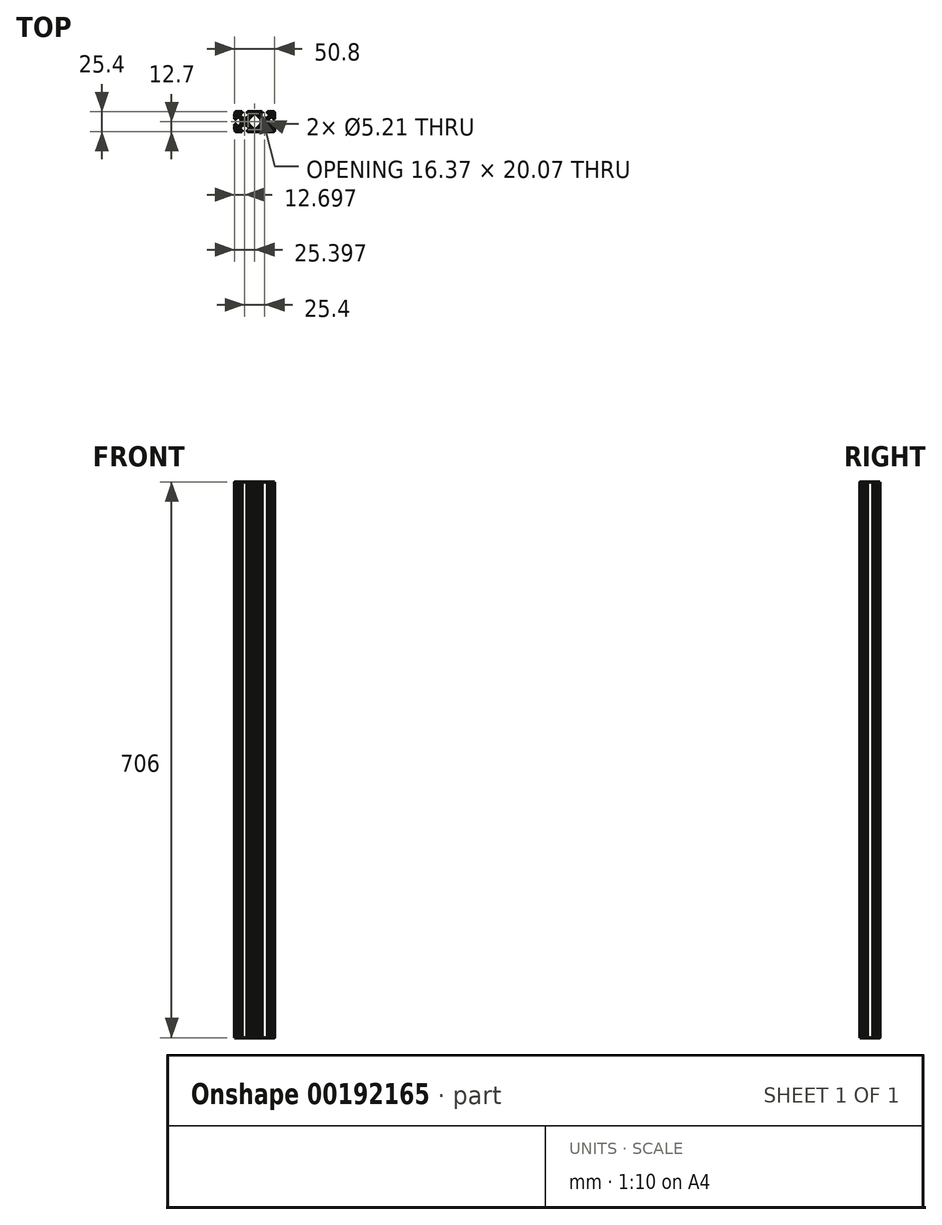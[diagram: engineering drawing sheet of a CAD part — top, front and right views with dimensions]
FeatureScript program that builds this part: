
annotation { "Feature Type Name" : "Feature", "Feature Type Description" : "" }
export const myFeature = defineFeature(function(context is Context, id is Id, definition is map)
    precondition{}
    {
        {
            var Q0;
            Q0=qCreatedBy(makeId("Top.planeOp"),FACE);
            var sketch = newSketch(context, id + "F0", { "sketchPlane" : qUnion([Q0])});
            skArc(sketch, "E0.0.0", {"start": v(22.53, 3.34) * mm, "mid": v(24.02, 3.96) * mm, "end": v(24.64, 5.45) * mm});
            skLineSegment(sketch, "E0.0.1", {"start": v(24.64, 5.45) * mm, "end": v(24.64, 5.47) * mm});
            skArc(sketch, "E0.0.2", {"start": v(24.64, 5.47) * mm, "mid": v(24.13, 5.98) * mm, "end": v(24.64, 6.49) * mm});
            skLineSegment(sketch, "E0.0.3", {"start": v(24.64, 6.49) * mm, "end": v(24.64, 9.72) * mm});
            skArc(sketch, "E0.0.4", {"start": v(24.64, 9.72) * mm, "mid": v(24.13, 10.22) * mm, "end": v(24.64, 10.73) * mm});
            skLineSegment(sketch, "E0.0.5", {"start": v(24.64, 10.73) * mm, "end": v(24.64, 11.68) * mm});
            skArc(sketch, "E0.0.6", {"start": v(24.64, 11.68) * mm, "mid": v(23.53, 12.79) * mm, "end": v(22.43, 11.68) * mm});
            skLineSegment(sketch, "E0.0.7", {"start": v(22.43, 11.68) * mm, "end": v(22.43, 9.67) * mm});
            skArc(sketch, "E0.0.8", {"start": v(22.43, 9.67) * mm, "mid": v(21.77, 8.7) * mm, "end": v(20.62, 8.92) * mm});
            skLineSegment(sketch, "E0.0.9", {"start": v(20.62, 8.92) * mm, "end": v(17.38, 12.16) * mm});
            skArc(sketch, "E0.0.10", {"start": v(17.38, 12.16) * mm, "mid": v(16.7, 13.19) * mm, "end": v(16.45, 14.4) * mm});
            skLineSegment(sketch, "E0.0.11", {"start": v(16.45, 14.4) * mm, "end": v(16.45, 17.68) * mm});
            skArc(sketch, "E0.0.12", {"start": v(16.45, 17.68) * mm, "mid": v(16.7, 18.9) * mm, "end": v(17.38, 19.92) * mm});
            skLineSegment(sketch, "E0.0.13", {"start": v(17.38, 19.92) * mm, "end": v(20.62, 23.16) * mm});
            skArc(sketch, "E0.0.14", {"start": v(20.62, 23.16) * mm, "mid": v(21.77, 23.39) * mm, "end": v(22.43, 22.41) * mm});
            skLineSegment(sketch, "E0.0.15", {"start": v(22.43, 22.41) * mm, "end": v(22.43, 20.4) * mm});
            skArc(sketch, "E0.0.16", {"start": v(22.43, 20.4) * mm, "mid": v(23.53, 19.3) * mm, "end": v(24.64, 20.4) * mm});
            skLineSegment(sketch, "E0.0.17", {"start": v(24.64, 20.4) * mm, "end": v(24.64, 21.35) * mm});
            skArc(sketch, "E0.0.18", {"start": v(24.64, 21.35) * mm, "mid": v(24.13, 21.86) * mm, "end": v(24.64, 22.36) * mm});
            skLineSegment(sketch, "E0.0.19", {"start": v(24.64, 22.36) * mm, "end": v(24.64, 25.6) * mm});
            skArc(sketch, "E0.0.20", {"start": v(24.64, 25.6) * mm, "mid": v(24.13, 26.1) * mm, "end": v(24.64, 26.6) * mm});
            skLineSegment(sketch, "E0.0.21", {"start": v(24.64, 26.6) * mm, "end": v(24.64, 26.63) * mm});
            skArc(sketch, "E0.0.22", {"start": v(24.64, 26.63) * mm, "mid": v(24.02, 28.12) * mm, "end": v(22.53, 28.74) * mm});
            skLineSegment(sketch, "E0.0.23", {"start": v(22.53, 28.74) * mm, "end": v(22.5, 28.74) * mm});
            skArc(sketch, "E0.0.24", {"start": v(22.5, 28.74) * mm, "mid": v(22, 28.23) * mm, "end": v(21.49, 28.74) * mm});
            skLineSegment(sketch, "E0.0.25", {"start": v(21.49, 28.74) * mm, "end": v(18.26, 28.74) * mm});
            skArc(sketch, "E0.0.26", {"start": v(18.26, 28.74) * mm, "mid": v(17.75, 28.23) * mm, "end": v(17.25, 28.74) * mm});
            skLineSegment(sketch, "E0.0.27", {"start": v(17.25, 28.74) * mm, "end": v(16.3, 28.74) * mm});
            skArc(sketch, "E0.0.28", {"start": v(16.3, 28.74) * mm, "mid": v(15.19, 27.64) * mm, "end": v(16.3, 26.53) * mm});
            skLineSegment(sketch, "E0.0.29", {"start": v(16.3, 26.53) * mm, "end": v(18.3, 26.53) * mm});
            skArc(sketch, "E0.0.30", {"start": v(18.3, 26.53) * mm, "mid": v(19.29, 25.88) * mm, "end": v(19.06, 24.72) * mm});
            skLineSegment(sketch, "E0.0.31", {"start": v(19.06, 24.72) * mm, "end": v(15.82, 21.49) * mm});
            skArc(sketch, "E0.0.32", {"start": v(15.82, 21.49) * mm, "mid": v(14.8, 20.8) * mm, "end": v(13.58, 20.56) * mm});
            skLineSegment(sketch, "E0.0.33", {"start": v(13.58, 20.56) * mm, "end": v(10.3, 20.56) * mm});
            skArc(sketch, "E0.0.34", {"start": v(10.3, 20.56) * mm, "mid": v(9.08, 20.8) * mm, "end": v(8.05, 21.49) * mm});
            skLineSegment(sketch, "E0.0.35", {"start": v(8.05, 21.49) * mm, "end": v(4.82, 24.72) * mm});
            skArc(sketch, "E0.0.36", {"start": v(4.82, 24.72) * mm, "mid": v(4.59, 25.88) * mm, "end": v(5.57, 26.53) * mm});
            skLineSegment(sketch, "E0.0.37", {"start": v(5.57, 26.53) * mm, "end": v(7.58, 26.53) * mm});
            skArc(sketch, "E0.0.38", {"start": v(7.58, 26.53) * mm, "mid": v(8.69, 27.64) * mm, "end": v(7.58, 28.74) * mm});
            skLineSegment(sketch, "E0.0.39", {"start": v(7.58, 28.74) * mm, "end": v(6.63, 28.74) * mm});
            skArc(sketch, "E0.0.40", {"start": v(6.63, 28.74) * mm, "mid": v(6.12, 28.23) * mm, "end": v(5.61, 28.74) * mm});
            skLineSegment(sketch, "E0.0.41", {"start": v(5.61, 28.74) * mm, "end": v(2.39, 28.74) * mm});
            skArc(sketch, "E0.0.42", {"start": v(2.39, 28.74) * mm, "mid": v(1.88, 28.23) * mm, "end": v(1.37, 28.74) * mm});
            skLineSegment(sketch, "E0.0.43", {"start": v(1.37, 28.74) * mm, "end": v(-2.9, 28.74) * mm});
            skArc(sketch, "E0.0.44", {"start": v(-2.9, 28.74) * mm, "mid": v(-3.4, 28.23) * mm, "end": v(-3.91, 28.74) * mm});
            skLineSegment(sketch, "E0.0.45", {"start": v(-3.91, 28.74) * mm, "end": v(-7.14, 28.74) * mm});
            skArc(sketch, "E0.0.46", {"start": v(-7.14, 28.74) * mm, "mid": v(-7.65, 28.23) * mm, "end": v(-8.15, 28.74) * mm});
            skLineSegment(sketch, "E0.0.47", {"start": v(-8.15, 28.74) * mm, "end": v(-9.1, 28.74) * mm});
            skArc(sketch, "E0.0.48", {"start": v(-9.1, 28.74) * mm, "mid": v(-10.21, 27.64) * mm, "end": v(-9.1, 26.53) * mm});
            skLineSegment(sketch, "E0.0.49", {"start": v(-9.1, 26.53) * mm, "end": v(-7.1, 26.53) * mm});
            skArc(sketch, "E0.0.50", {"start": v(-7.1, 26.53) * mm, "mid": v(-6.11, 25.88) * mm, "end": v(-6.34, 24.72) * mm});
            skLineSegment(sketch, "E0.0.51", {"start": v(-6.34, 24.72) * mm, "end": v(-9.58, 21.49) * mm});
            skArc(sketch, "E0.0.52", {"start": v(-9.58, 21.49) * mm, "mid": v(-10.6, 20.8) * mm, "end": v(-11.82, 20.56) * mm});
            skLineSegment(sketch, "E0.0.53", {"start": v(-11.82, 20.56) * mm, "end": v(-15.1, 20.56) * mm});
            skArc(sketch, "E0.0.54", {"start": v(-15.1, 20.56) * mm, "mid": v(-16.32, 20.8) * mm, "end": v(-17.35, 21.49) * mm});
            skLineSegment(sketch, "E0.0.55", {"start": v(-17.35, 21.49) * mm, "end": v(-20.58, 24.72) * mm});
            skArc(sketch, "E0.0.56", {"start": v(-20.58, 24.72) * mm, "mid": v(-20.81, 25.88) * mm, "end": v(-19.83, 26.53) * mm});
            skLineSegment(sketch, "E0.0.57", {"start": v(-19.83, 26.53) * mm, "end": v(-17.82, 26.53) * mm});
            skArc(sketch, "E0.0.58", {"start": v(-17.82, 26.53) * mm, "mid": v(-16.71, 27.64) * mm, "end": v(-17.82, 28.74) * mm});
            skLineSegment(sketch, "E0.0.59", {"start": v(-17.82, 28.74) * mm, "end": v(-18.77, 28.74) * mm});
            skArc(sketch, "E0.0.60", {"start": v(-18.77, 28.74) * mm, "mid": v(-19.28, 28.23) * mm, "end": v(-19.79, 28.74) * mm});
            skLineSegment(sketch, "E0.0.61", {"start": v(-19.79, 28.74) * mm, "end": v(-23.01, 28.74) * mm});
            skArc(sketch, "E0.0.62", {"start": v(-23.01, 28.74) * mm, "mid": v(-23.52, 28.23) * mm, "end": v(-24.03, 28.74) * mm});
            skLineSegment(sketch, "E0.0.63", {"start": v(-24.03, 28.74) * mm, "end": v(-24.05, 28.74) * mm});
            skArc(sketch, "E0.0.64", {"start": v(-24.05, 28.74) * mm, "mid": v(-25.55, 28.12) * mm, "end": v(-26.16, 26.63) * mm});
            skLineSegment(sketch, "E0.0.65", {"start": v(-26.16, 26.63) * mm, "end": v(-26.16, 26.6) * mm});
            skArc(sketch, "E0.0.66", {"start": v(-26.16, 26.6) * mm, "mid": v(-25.65, 26.1) * mm, "end": v(-26.16, 25.6) * mm});
            skLineSegment(sketch, "E0.0.67", {"start": v(-26.16, 25.6) * mm, "end": v(-26.16, 22.36) * mm});
            skArc(sketch, "E0.0.68", {"start": v(-26.16, 22.36) * mm, "mid": v(-25.65, 21.86) * mm, "end": v(-26.16, 21.35) * mm});
            skLineSegment(sketch, "E0.0.69", {"start": v(-26.16, 21.35) * mm, "end": v(-26.16, 20.4) * mm});
            skArc(sketch, "E0.0.70", {"start": v(-26.16, 20.4) * mm, "mid": v(-25.06, 19.3) * mm, "end": v(-23.95, 20.4) * mm});
            skLineSegment(sketch, "E0.0.71", {"start": v(-23.95, 20.4) * mm, "end": v(-23.95, 22.41) * mm});
            skArc(sketch, "E0.0.72", {"start": v(-23.95, 22.41) * mm, "mid": v(-23.3, 23.39) * mm, "end": v(-22.14, 23.16) * mm});
            skLineSegment(sketch, "E0.0.73", {"start": v(-22.14, 23.16) * mm, "end": v(-18.91, 19.92) * mm});
            skArc(sketch, "E0.0.74", {"start": v(-18.91, 19.92) * mm, "mid": v(-18.22, 18.9) * mm, "end": v(-17.98, 17.68) * mm});
            skLineSegment(sketch, "E0.0.75", {"start": v(-17.98, 17.68) * mm, "end": v(-17.98, 14.4) * mm});
            skArc(sketch, "E0.0.76", {"start": v(-17.98, 14.4) * mm, "mid": v(-18.22, 13.19) * mm, "end": v(-18.91, 12.16) * mm});
            skLineSegment(sketch, "E0.0.77", {"start": v(-18.91, 12.16) * mm, "end": v(-22.14, 8.92) * mm});
            skArc(sketch, "E0.0.78", {"start": v(-22.14, 8.92) * mm, "mid": v(-23.3, 8.7) * mm, "end": v(-23.95, 9.67) * mm});
            skLineSegment(sketch, "E0.0.79", {"start": v(-23.95, 9.67) * mm, "end": v(-23.95, 11.68) * mm});
            skArc(sketch, "E0.0.80", {"start": v(-23.95, 11.68) * mm, "mid": v(-25.06, 12.79) * mm, "end": v(-26.16, 11.68) * mm});
            skLineSegment(sketch, "E0.0.81", {"start": v(-26.16, 11.68) * mm, "end": v(-26.16, 10.73) * mm});
            skArc(sketch, "E0.0.82", {"start": v(-26.16, 10.73) * mm, "mid": v(-25.65, 10.22) * mm, "end": v(-26.16, 9.72) * mm});
            skLineSegment(sketch, "E0.0.83", {"start": v(-26.16, 9.72) * mm, "end": v(-26.16, 6.49) * mm});
            skArc(sketch, "E0.0.84", {"start": v(-26.16, 6.49) * mm, "mid": v(-25.65, 5.98) * mm, "end": v(-26.16, 5.47) * mm});
            skLineSegment(sketch, "E0.0.85", {"start": v(-26.16, 5.47) * mm, "end": v(-26.16, 5.45) * mm});
            skArc(sketch, "E0.0.86", {"start": v(-26.16, 5.45) * mm, "mid": v(-25.55, 3.96) * mm, "end": v(-24.05, 3.34) * mm});
            skLineSegment(sketch, "E0.0.87", {"start": v(-24.05, 3.34) * mm, "end": v(-24.03, 3.34) * mm});
            skArc(sketch, "E0.0.88", {"start": v(-24.03, 3.34) * mm, "mid": v(-23.52, 3.85) * mm, "end": v(-23.01, 3.34) * mm});
            skLineSegment(sketch, "E0.0.89", {"start": v(-23.01, 3.34) * mm, "end": v(-19.79, 3.34) * mm});
            skArc(sketch, "E0.0.90", {"start": v(-19.79, 3.34) * mm, "mid": v(-19.28, 3.85) * mm, "end": v(-18.77, 3.34) * mm});
            skLineSegment(sketch, "E0.0.91", {"start": v(-18.77, 3.34) * mm, "end": v(-17.82, 3.34) * mm});
            skArc(sketch, "E0.0.92", {"start": v(-17.82, 3.34) * mm, "mid": v(-16.71, 4.45) * mm, "end": v(-17.82, 5.55) * mm});
            skLineSegment(sketch, "E0.0.93", {"start": v(-17.82, 5.55) * mm, "end": v(-19.83, 5.55) * mm});
            skArc(sketch, "E0.0.94", {"start": v(-19.83, 5.55) * mm, "mid": v(-20.81, 6.2) * mm, "end": v(-20.58, 7.36) * mm});
            skLineSegment(sketch, "E0.0.95", {"start": v(-20.58, 7.36) * mm, "end": v(-17.35, 10.6) * mm});
            skArc(sketch, "E0.0.96", {"start": v(-17.35, 10.6) * mm, "mid": v(-16.32, 11.28) * mm, "end": v(-15.1, 11.52) * mm});
            skLineSegment(sketch, "E0.0.97", {"start": v(-15.1, 11.52) * mm, "end": v(-11.82, 11.52) * mm});
            skArc(sketch, "E0.0.98", {"start": v(-11.82, 11.52) * mm, "mid": v(-10.6, 11.28) * mm, "end": v(-9.58, 10.6) * mm});
            skLineSegment(sketch, "E0.0.99", {"start": v(-9.58, 10.6) * mm, "end": v(-6.34, 7.36) * mm});
            skArc(sketch, "E0.0.100", {"start": v(-6.34, 7.36) * mm, "mid": v(-6.11, 6.2) * mm, "end": v(-7.1, 5.55) * mm});
            skLineSegment(sketch, "E0.0.101", {"start": v(-7.1, 5.55) * mm, "end": v(-9.1, 5.55) * mm});
            skArc(sketch, "E0.0.102", {"start": v(-9.1, 5.55) * mm, "mid": v(-10.21, 4.45) * mm, "end": v(-9.1, 3.34) * mm});
            skLineSegment(sketch, "E0.0.103", {"start": v(-9.1, 3.34) * mm, "end": v(-8.15, 3.34) * mm});
            skArc(sketch, "E0.0.104", {"start": v(-8.15, 3.34) * mm, "mid": v(-7.65, 3.85) * mm, "end": v(-7.14, 3.34) * mm});
            skLineSegment(sketch, "E0.0.105", {"start": v(-7.14, 3.34) * mm, "end": v(-3.91, 3.34) * mm});
            skArc(sketch, "E0.0.106", {"start": v(-3.91, 3.34) * mm, "mid": v(-3.4, 3.85) * mm, "end": v(-2.9, 3.34) * mm});
            skLineSegment(sketch, "E0.0.107", {"start": v(-2.9, 3.34) * mm, "end": v(1.37, 3.34) * mm});
            skArc(sketch, "E0.0.108", {"start": v(1.37, 3.34) * mm, "mid": v(1.88, 3.85) * mm, "end": v(2.39, 3.34) * mm});
            skLineSegment(sketch, "E0.0.109", {"start": v(2.39, 3.34) * mm, "end": v(5.61, 3.34) * mm});
            skArc(sketch, "E0.0.110", {"start": v(5.61, 3.34) * mm, "mid": v(6.12, 3.85) * mm, "end": v(6.63, 3.34) * mm});
            skLineSegment(sketch, "E0.0.111", {"start": v(6.63, 3.34) * mm, "end": v(7.58, 3.34) * mm});
            skArc(sketch, "E0.0.112", {"start": v(7.58, 3.34) * mm, "mid": v(8.69, 4.45) * mm, "end": v(7.58, 5.55) * mm});
            skLineSegment(sketch, "E0.0.113", {"start": v(7.58, 5.55) * mm, "end": v(5.57, 5.55) * mm});
            skArc(sketch, "E0.0.114", {"start": v(5.57, 5.55) * mm, "mid": v(4.59, 6.2) * mm, "end": v(4.82, 7.36) * mm});
            skLineSegment(sketch, "E0.0.115", {"start": v(4.82, 7.36) * mm, "end": v(8.05, 10.6) * mm});
            skArc(sketch, "E0.0.116", {"start": v(8.05, 10.6) * mm, "mid": v(9.08, 11.28) * mm, "end": v(10.3, 11.52) * mm});
            skLineSegment(sketch, "E0.0.117", {"start": v(10.3, 11.52) * mm, "end": v(13.58, 11.52) * mm});
            skArc(sketch, "E0.0.118", {"start": v(13.58, 11.52) * mm, "mid": v(14.8, 11.28) * mm, "end": v(15.82, 10.6) * mm});
            skLineSegment(sketch, "E0.0.119", {"start": v(15.82, 10.6) * mm, "end": v(19.06, 7.36) * mm});
            skArc(sketch, "E0.0.120", {"start": v(19.06, 7.36) * mm, "mid": v(19.29, 6.2) * mm, "end": v(18.3, 5.55) * mm});
            skLineSegment(sketch, "E0.0.121", {"start": v(18.3, 5.55) * mm, "end": v(16.3, 5.55) * mm});
            skArc(sketch, "E0.0.122", {"start": v(16.3, 5.55) * mm, "mid": v(15.19, 4.45) * mm, "end": v(16.3, 3.34) * mm});
            skLineSegment(sketch, "E0.0.123", {"start": v(16.3, 3.34) * mm, "end": v(17.25, 3.34) * mm});
            skArc(sketch, "E0.0.124", {"start": v(17.25, 3.34) * mm, "mid": v(17.75, 3.85) * mm, "end": v(18.26, 3.34) * mm});
            skLineSegment(sketch, "E0.0.125", {"start": v(18.26, 3.34) * mm, "end": v(21.49, 3.34) * mm});
            skArc(sketch, "E0.0.126", {"start": v(21.49, 3.34) * mm, "mid": v(22, 3.85) * mm, "end": v(22.5, 3.34) * mm});
            skLineSegment(sketch, "E0.0.127", {"start": v(22.5, 3.34) * mm, "end": v(22.53, 3.34) * mm});
            skLineSegment(sketch, "E1.94", {"start": v(6.49, 19.92) * mm, "end": v(0.8, 25.61) * mm});
            skArc(sketch, "E1.114", {"start": v(-1.21, 26.07) * mm, "mid": v(-1.82, 25.95) * mm, "end": v(-2.33, 25.61) * mm});
            skArc(sketch, "E1.116", {"start": v(-2.33, 6.47) * mm, "mid": v(-1.82, 6.13) * mm, "end": v(-1.21, 6) * mm});
            skLineSegment(sketch, "E1.122", {"start": v(-0.31, 26.07) * mm, "end": v(-1.21, 26.07) * mm});
            skLineSegment(sketch, "E1.124", {"start": v(-8.02, 12.16) * mm, "end": v(-2.33, 6.47) * mm});
            skArc(sketch, "E1.133", {"start": v(-0.31, 6) * mm, "mid": v(0.3, 6.13) * mm, "end": v(0.8, 6.47) * mm});
            skArc(sketch, "E1.144", {"start": v(0.8, 25.61) * mm, "mid": v(0.3, 25.95) * mm, "end": v(-0.31, 26.07) * mm});
            skLineSegment(sketch, "E1.146", {"start": v(-1.21, 6) * mm, "end": v(-0.31, 6) * mm});
            skArc(sketch, "E1.157", {"start": v(6.49, 12.16) * mm, "mid": v(7.18, 13.19) * mm, "end": v(7.42, 14.4) * mm});
            skLineSegment(sketch, "E1.158", {"start": v(0.8, 6.47) * mm, "end": v(6.49, 12.16) * mm});
            skCircle(sketch, "E1.161", {"center": v(-13.46, 16.04) * mm, "radius": 2.6 * mm});
            skArc(sketch, "E1.163", {"start": v(7.42, 17.68) * mm, "mid": v(7.18, 18.9) * mm, "end": v(6.49, 19.92) * mm});
            skLineSegment(sketch, "E1.164", {"start": v(7.42, 14.4) * mm, "end": v(7.42, 17.68) * mm});
            skCircle(sketch, "E1.168", {"center": v(11.94, 16.04) * mm, "radius": 2.6 * mm});
            skArc(sketch, "E1.189", {"start": v(-8.02, 19.92) * mm, "mid": v(-8.7, 18.9) * mm, "end": v(-8.95, 17.68) * mm});
            skArc(sketch, "E1.206", {"start": v(-8.95, 14.4) * mm, "mid": v(-8.7, 13.19) * mm, "end": v(-8.02, 12.16) * mm});
            skLineSegment(sketch, "E1.207", {"start": v(-8.95, 17.68) * mm, "end": v(-8.95, 14.4) * mm});
            skLineSegment(sketch, "E1.208", {"start": v(-2.33, 25.61) * mm, "end": v(-8.02, 19.92) * mm});
            skSolve(sketch);
        }
        {
            var Q0;
            Q0=makeQuery(id+"F0.imprint","IMPRINT",FACE,{"disambiguationData":[TD([[makeQuery(id+"F0.imprint","IMPRINT",EDGE,{"derivedFrom":sQuery(id+"F0.wireOp",EDGE,"E1.94")}),-1.0]])]});
            var Q1;
            Q1=sQuery(id+"F0.wireOp",EDGE,"E0.0.0");
            var Q2;
            Q2=sQuery(id+"F0.wireOp",EDGE,"E0.0.1");
            var Q3;
            Q3=sQuery(id+"F0.wireOp",EDGE,"E0.0.2");
            var Q4;
            Q4=sQuery(id+"F0.wireOp",EDGE,"E0.0.3");
            var Q5;
            Q5=sQuery(id+"F0.wireOp",EDGE,"E0.0.4");
            var Q6;
            Q6=sQuery(id+"F0.wireOp",EDGE,"E0.0.5");
            var Q7;
            Q7=sQuery(id+"F0.wireOp",EDGE,"E0.0.6");
            var Q8;
            Q8=sQuery(id+"F0.wireOp",EDGE,"E0.0.7");
            var Q9;
            Q9=sQuery(id+"F0.wireOp",EDGE,"E0.0.8");
            var Q10;
            Q10=sQuery(id+"F0.wireOp",EDGE,"E0.0.9");
            var Q11;
            Q11=sQuery(id+"F0.wireOp",EDGE,"E0.0.10");
            var Q12;
            Q12=sQuery(id+"F0.wireOp",EDGE,"E0.0.11");
            var Q13;
            Q13=sQuery(id+"F0.wireOp",EDGE,"E0.0.12");
            var Q14;
            Q14=sQuery(id+"F0.wireOp",EDGE,"E0.0.13");
            var Q15;
            Q15=sQuery(id+"F0.wireOp",EDGE,"E0.0.14");
            var Q16;
            Q16=sQuery(id+"F0.wireOp",EDGE,"E0.0.15");
            var Q17;
            Q17=sQuery(id+"F0.wireOp",EDGE,"E0.0.16");
            var Q18;
            Q18=sQuery(id+"F0.wireOp",EDGE,"E0.0.17");
            var Q19;
            Q19=sQuery(id+"F0.wireOp",EDGE,"E0.0.18");
            var Q20;
            Q20=sQuery(id+"F0.wireOp",EDGE,"E0.0.19");
            var Q21;
            Q21=sQuery(id+"F0.wireOp",EDGE,"E0.0.20");
            var Q22;
            Q22=sQuery(id+"F0.wireOp",EDGE,"E0.0.21");
            var Q23;
            Q23=sQuery(id+"F0.wireOp",EDGE,"E0.0.22");
            var Q24;
            Q24=sQuery(id+"F0.wireOp",EDGE,"E0.0.23");
            var Q25;
            Q25=sQuery(id+"F0.wireOp",EDGE,"E0.0.24");
            var Q26;
            Q26=sQuery(id+"F0.wireOp",EDGE,"E0.0.25");
            var Q27;
            Q27=sQuery(id+"F0.wireOp",EDGE,"E0.0.26");
            var Q28;
            Q28=sQuery(id+"F0.wireOp",EDGE,"E0.0.27");
            var Q29;
            Q29=sQuery(id+"F0.wireOp",EDGE,"E0.0.28");
            var Q30;
            Q30=sQuery(id+"F0.wireOp",EDGE,"E0.0.29");
            var Q31;
            Q31=sQuery(id+"F0.wireOp",EDGE,"E0.0.30");
            var Q32;
            Q32=sQuery(id+"F0.wireOp",EDGE,"E0.0.31");
            var Q33;
            Q33=sQuery(id+"F0.wireOp",EDGE,"E0.0.32");
            var Q34;
            Q34=sQuery(id+"F0.wireOp",EDGE,"E0.0.33");
            var Q35;
            Q35=sQuery(id+"F0.wireOp",EDGE,"E0.0.34");
            var Q36;
            Q36=sQuery(id+"F0.wireOp",EDGE,"E0.0.35");
            var Q37;
            Q37=sQuery(id+"F0.wireOp",EDGE,"E0.0.36");
            var Q38;
            Q38=sQuery(id+"F0.wireOp",EDGE,"E0.0.37");
            var Q39;
            Q39=sQuery(id+"F0.wireOp",EDGE,"E0.0.38");
            var Q40;
            Q40=sQuery(id+"F0.wireOp",EDGE,"E0.0.39");
            var Q41;
            Q41=sQuery(id+"F0.wireOp",EDGE,"E0.0.40");
            var Q42;
            Q42=sQuery(id+"F0.wireOp",EDGE,"E0.0.41");
            var Q43;
            Q43=sQuery(id+"F0.wireOp",EDGE,"E0.0.42");
            var Q44;
            Q44=sQuery(id+"F0.wireOp",EDGE,"E0.0.43");
            var Q45;
            Q45=sQuery(id+"F0.wireOp",EDGE,"E0.0.44");
            var Q46;
            Q46=sQuery(id+"F0.wireOp",EDGE,"E0.0.45");
            var Q47;
            Q47=sQuery(id+"F0.wireOp",EDGE,"E0.0.46");
            var Q48;
            Q48=sQuery(id+"F0.wireOp",EDGE,"E0.0.47");
            var Q49;
            Q49=sQuery(id+"F0.wireOp",EDGE,"E0.0.48");
            var Q50;
            Q50=sQuery(id+"F0.wireOp",EDGE,"E0.0.49");
            var Q51;
            Q51=sQuery(id+"F0.wireOp",EDGE,"E0.0.50");
            var Q52;
            Q52=sQuery(id+"F0.wireOp",EDGE,"E0.0.51");
            var Q53;
            Q53=sQuery(id+"F0.wireOp",EDGE,"E0.0.52");
            var Q54;
            Q54=sQuery(id+"F0.wireOp",EDGE,"E0.0.53");
            var Q55;
            Q55=sQuery(id+"F0.wireOp",EDGE,"E0.0.54");
            var Q56;
            Q56=sQuery(id+"F0.wireOp",EDGE,"E0.0.55");
            var Q57;
            Q57=sQuery(id+"F0.wireOp",EDGE,"E0.0.56");
            var Q58;
            Q58=sQuery(id+"F0.wireOp",EDGE,"E0.0.57");
            var Q59;
            Q59=sQuery(id+"F0.wireOp",EDGE,"E0.0.58");
            var Q60;
            Q60=sQuery(id+"F0.wireOp",EDGE,"E0.0.59");
            var Q61;
            Q61=sQuery(id+"F0.wireOp",EDGE,"E0.0.60");
            var Q62;
            Q62=sQuery(id+"F0.wireOp",EDGE,"E0.0.61");
            var Q63;
            Q63=sQuery(id+"F0.wireOp",EDGE,"E0.0.62");
            var Q64;
            Q64=sQuery(id+"F0.wireOp",EDGE,"E0.0.63");
            var Q65;
            Q65=sQuery(id+"F0.wireOp",EDGE,"E0.0.64");
            var Q66;
            Q66=sQuery(id+"F0.wireOp",EDGE,"E0.0.65");
            var Q67;
            Q67=sQuery(id+"F0.wireOp",EDGE,"E0.0.66");
            var Q68;
            Q68=sQuery(id+"F0.wireOp",EDGE,"E0.0.67");
            var Q69;
            Q69=sQuery(id+"F0.wireOp",EDGE,"E0.0.68");
            var Q70;
            Q70=sQuery(id+"F0.wireOp",EDGE,"E0.0.69");
            var Q71;
            Q71=sQuery(id+"F0.wireOp",EDGE,"E0.0.70");
            var Q72;
            Q72=sQuery(id+"F0.wireOp",EDGE,"E0.0.71");
            var Q73;
            Q73=sQuery(id+"F0.wireOp",EDGE,"E0.0.72");
            var Q74;
            Q74=sQuery(id+"F0.wireOp",EDGE,"E0.0.73");
            var Q75;
            Q75=sQuery(id+"F0.wireOp",EDGE,"E0.0.74");
            var Q76;
            Q76=sQuery(id+"F0.wireOp",EDGE,"E0.0.75");
            var Q77;
            Q77=sQuery(id+"F0.wireOp",EDGE,"E0.0.76");
            var Q78;
            Q78=sQuery(id+"F0.wireOp",EDGE,"E0.0.77");
            var Q79;
            Q79=sQuery(id+"F0.wireOp",EDGE,"E0.0.78");
            var Q80;
            Q80=sQuery(id+"F0.wireOp",EDGE,"E0.0.79");
            var Q81;
            Q81=sQuery(id+"F0.wireOp",EDGE,"E0.0.80");
            var Q82;
            Q82=sQuery(id+"F0.wireOp",EDGE,"E0.0.81");
            var Q83;
            Q83=sQuery(id+"F0.wireOp",EDGE,"E0.0.82");
            var Q84;
            Q84=sQuery(id+"F0.wireOp",EDGE,"E0.0.83");
            var Q85;
            Q85=sQuery(id+"F0.wireOp",EDGE,"E0.0.84");
            var Q86;
            Q86=sQuery(id+"F0.wireOp",EDGE,"E0.0.85");
            var Q87;
            Q87=sQuery(id+"F0.wireOp",EDGE,"E0.0.86");
            var Q88;
            Q88=sQuery(id+"F0.wireOp",EDGE,"E0.0.87");
            var Q89;
            Q89=sQuery(id+"F0.wireOp",EDGE,"E0.0.88");
            var Q90;
            Q90=sQuery(id+"F0.wireOp",EDGE,"E0.0.89");
            var Q91;
            Q91=sQuery(id+"F0.wireOp",EDGE,"E0.0.90");
            var Q92;
            Q92=sQuery(id+"F0.wireOp",EDGE,"E0.0.91");
            var Q93;
            Q93=sQuery(id+"F0.wireOp",EDGE,"E0.0.92");
            var Q94;
            Q94=sQuery(id+"F0.wireOp",EDGE,"E0.0.93");
            var Q95;
            Q95=sQuery(id+"F0.wireOp",EDGE,"E0.0.94");
            var Q96;
            Q96=sQuery(id+"F0.wireOp",EDGE,"E0.0.95");
            var Q97;
            Q97=sQuery(id+"F0.wireOp",EDGE,"E0.0.96");
            var Q98;
            Q98=sQuery(id+"F0.wireOp",EDGE,"E0.0.97");
            var Q99;
            Q99=sQuery(id+"F0.wireOp",EDGE,"E0.0.98");
            var Q100;
            Q100=sQuery(id+"F0.wireOp",EDGE,"E0.0.99");
            var Q101;
            Q101=sQuery(id+"F0.wireOp",EDGE,"E0.0.100");
            var Q102;
            Q102=sQuery(id+"F0.wireOp",EDGE,"E0.0.101");
            var Q103;
            Q103=sQuery(id+"F0.wireOp",EDGE,"E0.0.102");
            var Q104;
            Q104=sQuery(id+"F0.wireOp",EDGE,"E0.0.103");
            var Q105;
            Q105=sQuery(id+"F0.wireOp",EDGE,"E0.0.104");
            var Q106;
            Q106=sQuery(id+"F0.wireOp",EDGE,"E0.0.105");
            var Q107;
            Q107=sQuery(id+"F0.wireOp",EDGE,"E0.0.106");
            var Q108;
            Q108=sQuery(id+"F0.wireOp",EDGE,"E0.0.107");
            var Q109;
            Q109=sQuery(id+"F0.wireOp",EDGE,"E0.0.108");
            var Q110;
            Q110=sQuery(id+"F0.wireOp",EDGE,"E0.0.109");
            var Q111;
            Q111=sQuery(id+"F0.wireOp",EDGE,"E0.0.110");
            var Q112;
            Q112=sQuery(id+"F0.wireOp",EDGE,"E0.0.111");
            var Q113;
            Q113=sQuery(id+"F0.wireOp",EDGE,"E0.0.112");
            var Q114;
            Q114=sQuery(id+"F0.wireOp",EDGE,"E0.0.113");
            var Q115;
            Q115=sQuery(id+"F0.wireOp",EDGE,"E0.0.114");
            var Q116;
            Q116=sQuery(id+"F0.wireOp",EDGE,"E0.0.115");
            var Q117;
            Q117=sQuery(id+"F0.wireOp",EDGE,"E0.0.116");
            var Q118;
            Q118=sQuery(id+"F0.wireOp",EDGE,"E0.0.117");
            var Q119;
            Q119=sQuery(id+"F0.wireOp",EDGE,"E0.0.118");
            var Q120;
            Q120=sQuery(id+"F0.wireOp",EDGE,"E0.0.119");
            var Q121;
            Q121=sQuery(id+"F0.wireOp",EDGE,"E0.0.120");
            var Q122;
            Q122=sQuery(id+"F0.wireOp",EDGE,"E0.0.121");
            var Q123;
            Q123=sQuery(id+"F0.wireOp",EDGE,"E0.0.122");
            var Q124;
            Q124=sQuery(id+"F0.wireOp",EDGE,"E0.0.123");
            var Q125;
            Q125=sQuery(id+"F0.wireOp",EDGE,"E0.0.124");
            var Q126;
            Q126=sQuery(id+"F0.wireOp",EDGE,"E0.0.125");
            var Q127;
            Q127=sQuery(id+"F0.wireOp",EDGE,"E0.0.126");
            var Q128;
            Q128=sQuery(id+"F0.wireOp",EDGE,"E0.0.127");
            var Q129;
            Q129=sQuery(id+"F0.wireOp",EDGE,"E0.0.0");
            var Q130;
            Q130=sQuery(id+"F0.wireOp",EDGE,"E0.0.1");
            var Q131;
            Q131=sQuery(id+"F0.wireOp",EDGE,"E0.0.2");
            var Q132;
            Q132=sQuery(id+"F0.wireOp",EDGE,"E0.0.3");
            var Q133;
            Q133=sQuery(id+"F0.wireOp",EDGE,"E0.0.4");
            var Q134;
            Q134=sQuery(id+"F0.wireOp",EDGE,"E0.0.5");
            var Q135;
            Q135=sQuery(id+"F0.wireOp",EDGE,"E0.0.6");
            var Q136;
            Q136=sQuery(id+"F0.wireOp",EDGE,"E0.0.7");
            var Q137;
            Q137=sQuery(id+"F0.wireOp",EDGE,"E0.0.8");
            var Q138;
            Q138=sQuery(id+"F0.wireOp",EDGE,"E0.0.9");
            var Q139;
            Q139=sQuery(id+"F0.wireOp",EDGE,"E0.0.10");
            var Q140;
            Q140=sQuery(id+"F0.wireOp",EDGE,"E0.0.11");
            var Q141;
            Q141=sQuery(id+"F0.wireOp",EDGE,"E0.0.12");
            var Q142;
            Q142=sQuery(id+"F0.wireOp",EDGE,"E0.0.13");
            var Q143;
            Q143=sQuery(id+"F0.wireOp",EDGE,"E0.0.14");
            var Q144;
            Q144=sQuery(id+"F0.wireOp",EDGE,"E0.0.15");
            var Q145;
            Q145=sQuery(id+"F0.wireOp",EDGE,"E0.0.16");
            var Q146;
            Q146=sQuery(id+"F0.wireOp",EDGE,"E0.0.17");
            var Q147;
            Q147=sQuery(id+"F0.wireOp",EDGE,"E0.0.18");
            var Q148;
            Q148=sQuery(id+"F0.wireOp",EDGE,"E0.0.19");
            var Q149;
            Q149=sQuery(id+"F0.wireOp",EDGE,"E0.0.20");
            var Q150;
            Q150=sQuery(id+"F0.wireOp",EDGE,"E0.0.21");
            var Q151;
            Q151=sQuery(id+"F0.wireOp",EDGE,"E0.0.22");
            var Q152;
            Q152=sQuery(id+"F0.wireOp",EDGE,"E0.0.23");
            var Q153;
            Q153=sQuery(id+"F0.wireOp",EDGE,"E0.0.24");
            var Q154;
            Q154=sQuery(id+"F0.wireOp",EDGE,"E0.0.25");
            var Q155;
            Q155=sQuery(id+"F0.wireOp",EDGE,"E0.0.26");
            var Q156;
            Q156=sQuery(id+"F0.wireOp",EDGE,"E0.0.27");
            var Q157;
            Q157=sQuery(id+"F0.wireOp",EDGE,"E0.0.28");
            var Q158;
            Q158=sQuery(id+"F0.wireOp",EDGE,"E0.0.29");
            var Q159;
            Q159=sQuery(id+"F0.wireOp",EDGE,"E0.0.30");
            var Q160;
            Q160=sQuery(id+"F0.wireOp",EDGE,"E0.0.31");
            var Q161;
            Q161=sQuery(id+"F0.wireOp",EDGE,"E0.0.32");
            var Q162;
            Q162=sQuery(id+"F0.wireOp",EDGE,"E0.0.33");
            var Q163;
            Q163=sQuery(id+"F0.wireOp",EDGE,"E0.0.34");
            var Q164;
            Q164=sQuery(id+"F0.wireOp",EDGE,"E0.0.35");
            var Q165;
            Q165=sQuery(id+"F0.wireOp",EDGE,"E0.0.36");
            var Q166;
            Q166=sQuery(id+"F0.wireOp",EDGE,"E0.0.37");
            var Q167;
            Q167=sQuery(id+"F0.wireOp",EDGE,"E0.0.38");
            var Q168;
            Q168=sQuery(id+"F0.wireOp",EDGE,"E0.0.39");
            var Q169;
            Q169=sQuery(id+"F0.wireOp",EDGE,"E0.0.40");
            var Q170;
            Q170=sQuery(id+"F0.wireOp",EDGE,"E0.0.41");
            var Q171;
            Q171=sQuery(id+"F0.wireOp",EDGE,"E0.0.42");
            var Q172;
            Q172=sQuery(id+"F0.wireOp",EDGE,"E0.0.43");
            var Q173;
            Q173=sQuery(id+"F0.wireOp",EDGE,"E0.0.44");
            var Q174;
            Q174=sQuery(id+"F0.wireOp",EDGE,"E0.0.45");
            var Q175;
            Q175=sQuery(id+"F0.wireOp",EDGE,"E0.0.46");
            var Q176;
            Q176=sQuery(id+"F0.wireOp",EDGE,"E0.0.47");
            var Q177;
            Q177=sQuery(id+"F0.wireOp",EDGE,"E0.0.48");
            var Q178;
            Q178=sQuery(id+"F0.wireOp",EDGE,"E0.0.49");
            var Q179;
            Q179=sQuery(id+"F0.wireOp",EDGE,"E0.0.50");
            var Q180;
            Q180=sQuery(id+"F0.wireOp",EDGE,"E0.0.51");
            var Q181;
            Q181=sQuery(id+"F0.wireOp",EDGE,"E0.0.52");
            var Q182;
            Q182=sQuery(id+"F0.wireOp",EDGE,"E0.0.53");
            var Q183;
            Q183=sQuery(id+"F0.wireOp",EDGE,"E0.0.54");
            var Q184;
            Q184=sQuery(id+"F0.wireOp",EDGE,"E0.0.55");
            var Q185;
            Q185=sQuery(id+"F0.wireOp",EDGE,"E0.0.56");
            var Q186;
            Q186=sQuery(id+"F0.wireOp",EDGE,"E0.0.57");
            var Q187;
            Q187=sQuery(id+"F0.wireOp",EDGE,"E0.0.58");
            var Q188;
            Q188=sQuery(id+"F0.wireOp",EDGE,"E0.0.59");
            var Q189;
            Q189=sQuery(id+"F0.wireOp",EDGE,"E0.0.60");
            var Q190;
            Q190=sQuery(id+"F0.wireOp",EDGE,"E0.0.61");
            var Q191;
            Q191=sQuery(id+"F0.wireOp",EDGE,"E0.0.62");
            var Q192;
            Q192=sQuery(id+"F0.wireOp",EDGE,"E0.0.63");
            var Q193;
            Q193=sQuery(id+"F0.wireOp",EDGE,"E0.0.64");
            var Q194;
            Q194=sQuery(id+"F0.wireOp",EDGE,"E0.0.65");
            var Q195;
            Q195=sQuery(id+"F0.wireOp",EDGE,"E0.0.66");
            var Q196;
            Q196=sQuery(id+"F0.wireOp",EDGE,"E0.0.67");
            var Q197;
            Q197=sQuery(id+"F0.wireOp",EDGE,"E0.0.68");
            var Q198;
            Q198=sQuery(id+"F0.wireOp",EDGE,"E0.0.69");
            var Q199;
            Q199=sQuery(id+"F0.wireOp",EDGE,"E0.0.70");
            var Q200;
            Q200=sQuery(id+"F0.wireOp",EDGE,"E0.0.71");
            var Q201;
            Q201=sQuery(id+"F0.wireOp",EDGE,"E0.0.72");
            var Q202;
            Q202=sQuery(id+"F0.wireOp",EDGE,"E0.0.73");
            var Q203;
            Q203=sQuery(id+"F0.wireOp",EDGE,"E0.0.74");
            var Q204;
            Q204=sQuery(id+"F0.wireOp",EDGE,"E0.0.75");
            var Q205;
            Q205=sQuery(id+"F0.wireOp",EDGE,"E0.0.76");
            var Q206;
            Q206=sQuery(id+"F0.wireOp",EDGE,"E0.0.77");
            var Q207;
            Q207=sQuery(id+"F0.wireOp",EDGE,"E0.0.78");
            var Q208;
            Q208=sQuery(id+"F0.wireOp",EDGE,"E0.0.79");
            var Q209;
            Q209=sQuery(id+"F0.wireOp",EDGE,"E0.0.80");
            var Q210;
            Q210=sQuery(id+"F0.wireOp",EDGE,"E0.0.81");
            var Q211;
            Q211=sQuery(id+"F0.wireOp",EDGE,"E0.0.82");
            var Q212;
            Q212=sQuery(id+"F0.wireOp",EDGE,"E0.0.83");
            var Q213;
            Q213=sQuery(id+"F0.wireOp",EDGE,"E0.0.84");
            var Q214;
            Q214=sQuery(id+"F0.wireOp",EDGE,"E0.0.85");
            var Q215;
            Q215=sQuery(id+"F0.wireOp",EDGE,"E0.0.86");
            var Q216;
            Q216=sQuery(id+"F0.wireOp",EDGE,"E0.0.87");
            var Q217;
            Q217=sQuery(id+"F0.wireOp",EDGE,"E0.0.88");
            var Q218;
            Q218=sQuery(id+"F0.wireOp",EDGE,"E0.0.89");
            var Q219;
            Q219=sQuery(id+"F0.wireOp",EDGE,"E0.0.90");
            var Q220;
            Q220=sQuery(id+"F0.wireOp",EDGE,"E0.0.91");
            var Q221;
            Q221=sQuery(id+"F0.wireOp",EDGE,"E0.0.92");
            var Q222;
            Q222=sQuery(id+"F0.wireOp",EDGE,"E0.0.93");
            var Q223;
            Q223=sQuery(id+"F0.wireOp",EDGE,"E0.0.94");
            var Q224;
            Q224=sQuery(id+"F0.wireOp",EDGE,"E0.0.95");
            var Q225;
            Q225=sQuery(id+"F0.wireOp",EDGE,"E0.0.96");
            var Q226;
            Q226=sQuery(id+"F0.wireOp",EDGE,"E0.0.97");
            var Q227;
            Q227=sQuery(id+"F0.wireOp",EDGE,"E0.0.98");
            var Q228;
            Q228=sQuery(id+"F0.wireOp",EDGE,"E0.0.99");
            var Q229;
            Q229=sQuery(id+"F0.wireOp",EDGE,"E0.0.100");
            var Q230;
            Q230=sQuery(id+"F0.wireOp",EDGE,"E0.0.101");
            var Q231;
            Q231=sQuery(id+"F0.wireOp",EDGE,"E0.0.102");
            var Q232;
            Q232=sQuery(id+"F0.wireOp",EDGE,"E0.0.103");
            var Q233;
            Q233=sQuery(id+"F0.wireOp",EDGE,"E0.0.104");
            var Q234;
            Q234=sQuery(id+"F0.wireOp",EDGE,"E0.0.105");
            var Q235;
            Q235=sQuery(id+"F0.wireOp",EDGE,"E0.0.106");
            var Q236;
            Q236=sQuery(id+"F0.wireOp",EDGE,"E0.0.107");
            var Q237;
            Q237=sQuery(id+"F0.wireOp",EDGE,"E0.0.108");
            var Q238;
            Q238=sQuery(id+"F0.wireOp",EDGE,"E0.0.109");
            var Q239;
            Q239=sQuery(id+"F0.wireOp",EDGE,"E0.0.110");
            var Q240;
            Q240=sQuery(id+"F0.wireOp",EDGE,"E0.0.111");
            var Q241;
            Q241=sQuery(id+"F0.wireOp",EDGE,"E0.0.112");
            var Q242;
            Q242=sQuery(id+"F0.wireOp",EDGE,"E0.0.113");
            var Q243;
            Q243=sQuery(id+"F0.wireOp",EDGE,"E0.0.114");
            var Q244;
            Q244=sQuery(id+"F0.wireOp",EDGE,"E0.0.115");
            var Q245;
            Q245=sQuery(id+"F0.wireOp",EDGE,"E0.0.116");
            var Q246;
            Q246=sQuery(id+"F0.wireOp",EDGE,"E0.0.117");
            var Q247;
            Q247=sQuery(id+"F0.wireOp",EDGE,"E0.0.118");
            var Q248;
            Q248=sQuery(id+"F0.wireOp",EDGE,"E0.0.119");
            var Q249;
            Q249=sQuery(id+"F0.wireOp",EDGE,"E0.0.120");
            var Q250;
            Q250=sQuery(id+"F0.wireOp",EDGE,"E0.0.121");
            var Q251;
            Q251=sQuery(id+"F0.wireOp",EDGE,"E0.0.122");
            var Q252;
            Q252=sQuery(id+"F0.wireOp",EDGE,"E0.0.123");
            var Q253;
            Q253=sQuery(id+"F0.wireOp",EDGE,"E0.0.124");
            var Q254;
            Q254=sQuery(id+"F0.wireOp",EDGE,"E0.0.125");
            var Q255;
            Q255=sQuery(id+"F0.wireOp",EDGE,"E0.0.126");
            var Q256;
            Q256=sQuery(id+"F0.wireOp",EDGE,"E0.0.127");
            var Q257;
            Q257=sQuery(id+"F0.wireOp",EDGE,"E1.94");
            var Q258;
            Q258=sQuery(id+"F0.wireOp",EDGE,"E0.0.41");
            var Q259;
            Q259=sQuery(id+"F0.wireOp",EDGE,"E0.0.105");
            var Q260;
            Q260=sQuery(id+"F0.wireOp",EDGE,"E1.114");
            var Q261;
            Q261=sQuery(id+"F0.wireOp",EDGE,"E1.116");
            var Q262;
            Q262=sQuery(id+"F0.wireOp",EDGE,"E0.0.107");
            var Q263;
            Q263=sQuery(id+"F0.wireOp",EDGE,"E1.122");
            var Q264;
            Q264=sQuery(id+"F0.wireOp",EDGE,"E1.124");
            var Q265;
            Q265=sQuery(id+"F0.wireOp",EDGE,"E1.133");
            var Q266;
            Q266=sQuery(id+"F0.wireOp",EDGE,"E0.0.43");
            var Q267;
            Q267=sQuery(id+"F0.wireOp",EDGE,"E1.144");
            var Q268;
            Q268=sQuery(id+"F0.wireOp",EDGE,"E1.146");
            var Q269;
            Q269=sQuery(id+"F0.wireOp",EDGE,"E0.0.117");
            var Q270;
            Q270=sQuery(id+"F0.wireOp",EDGE,"E0.0.42");
            var Q271;
            Q271=sQuery(id+"F0.wireOp",EDGE,"E0.0.97");
            var Q272;
            Q272=sQuery(id+"F0.wireOp",EDGE,"E0.0.106");
            var Q273;
            Q273=sQuery(id+"F0.wireOp",EDGE,"E0.0.109");
            var Q274;
            Q274=sQuery(id+"F0.wireOp",EDGE,"E0.0.114");
            var Q275;
            Q275=sQuery(id+"F0.wireOp",EDGE,"E1.157");
            var Q276;
            Q276=sQuery(id+"F0.wireOp",EDGE,"E1.158");
            var Q277;
            Q277=sQuery(id+"F0.wireOp",EDGE,"E0.0.33");
            var Q278;
            Q278=sQuery(id+"F0.wireOp",EDGE,"E0.0.115");
            var Q279;
            Q279=sQuery(id+"F0.wireOp",EDGE,"E1.163");
            var Q280;
            Q280=sQuery(id+"F0.wireOp",EDGE,"E1.164");
            var Q281;
            Q281=sQuery(id+"F0.wireOp",EDGE,"E0.0.112");
            var Q282;
            Q282=sQuery(id+"F0.wireOp",EDGE,"E0.0.34");
            var Q283;
            Q283=sQuery(id+"F0.wireOp",EDGE,"E1.168");
            var Q284;
            Q284=sQuery(id+"F0.wireOp",EDGE,"E0.0.28");
            var Q285;
            Q285=sQuery(id+"F0.wireOp",EDGE,"E0.0.35");
            var Q286;
            Q286=sQuery(id+"F0.wireOp",EDGE,"E0.0.38");
            var Q287;
            Q287=sQuery(id+"F0.wireOp",EDGE,"E0.0.48");
            var Q288;
            Q288=sQuery(id+"F0.wireOp",EDGE,"E0.0.52");
            var Q289;
            Q289=sQuery(id+"F0.wireOp",EDGE,"E0.0.53");
            var Q290;
            Q290=sQuery(id+"F0.wireOp",EDGE,"E0.0.98");
            var Q291;
            Q291=sQuery(id+"F0.wireOp",EDGE,"E0.0.108");
            var Q292;
            Q292=sQuery(id+"F0.wireOp",EDGE,"E0.0.113");
            var Q293;
            Q293=sQuery(id+"F0.wireOp",EDGE,"E0.0.116");
            var Q294;
            Q294=sQuery(id+"F0.wireOp",EDGE,"E0.0.96");
            var Q295;
            Q295=sQuery(id+"F0.wireOp",EDGE,"E0.0.92");
            var Q296;
            Q296=sQuery(id+"F0.wireOp",EDGE,"E0.0.32");
            var Q297;
            Q297=sQuery(id+"F0.wireOp",EDGE,"E0.0.37");
            var Q298;
            Q298=sQuery(id+"F0.wireOp",EDGE,"E0.0.111");
            var Q299;
            Q299=sQuery(id+"F0.wireOp",EDGE,"E0.0.39");
            var Q300;
            Q300=sQuery(id+"F0.wireOp",EDGE,"E0.0.90");
            var Q301;
            Q301=sQuery(id+"F0.wireOp",EDGE,"E0.0.44");
            var Q302;
            Q302=sQuery(id+"F0.wireOp",EDGE,"E1.189");
            var Q303;
            Q303=sQuery(id+"F0.wireOp",EDGE,"E0.0.29");
            var Q304;
            Q304=sQuery(id+"F0.wireOp",EDGE,"E0.0.102");
            var Q305;
            Q305=sQuery(id+"F0.wireOp",EDGE,"E0.0.54");
            var Q306;
            Q306=sQuery(id+"F0.wireOp",EDGE,"E0.0.31");
            var Q307;
            Q307=sQuery(id+"F0.wireOp",EDGE,"E0.0.36");
            var Q308;
            Q308=sQuery(id+"F0.wireOp",EDGE,"E0.0.40");
            var Q309;
            Q309=sQuery(id+"F0.wireOp",EDGE,"E0.0.47");
            var Q310;
            Q310=sQuery(id+"F0.wireOp",EDGE,"E0.0.49");
            var Q311;
            Q311=sQuery(id+"F0.wireOp",EDGE,"E0.0.50");
            var Q312;
            Q312=sQuery(id+"F0.wireOp",EDGE,"E0.0.51");
            var Q313;
            Q313=sQuery(id+"F0.wireOp",EDGE,"E0.0.118");
            var Q314;
            Q314=sQuery(id+"F0.wireOp",EDGE,"E0.0.91");
            var Q315;
            Q315=sQuery(id+"F0.wireOp",EDGE,"E0.0.95");
            var Q316;
            Q316=sQuery(id+"F0.wireOp",EDGE,"E0.0.99");
            var Q317;
            Q317=sQuery(id+"F0.wireOp",EDGE,"E0.0.100");
            var Q318;
            Q318=sQuery(id+"F0.wireOp",EDGE,"E0.0.110");
            var Q319;
            Q319=sQuery(id+"F0.wireOp",EDGE,"E1.206");
            var Q320;
            Q320=sQuery(id+"F0.wireOp",EDGE,"E1.207");
            var Q321;
            Q321=sQuery(id+"F0.wireOp",EDGE,"E1.208");
            var Q322;
            Q322=sQuery(id+"F0.wireOp",EDGE,"E0.0.27");
            var Q323;
            Q323=sQuery(id+"F0.wireOp",EDGE,"E0.0.104");
            var Q324;
            Q324=sQuery(id+"F0.wireOp",EDGE,"E0.0.26");
            var Q325;
            Q325=sQuery(id+"F0.wireOp",EDGE,"E0.0.45");
            var Q326;
            Q326=sQuery(id+"F0.wireOp",EDGE,"E0.0.46");
            var Q327;
            Q327=sQuery(id+"F0.wireOp",EDGE,"E0.0.93");
            var Q328;
            Q328=sQuery(id+"F0.wireOp",EDGE,"E0.0.78");
            var Q329;
            Q329=sQuery(id+"F0.wireOp",EDGE,"E0.0.24");
            var Q330;
            Q330=sQuery(id+"F0.wireOp",EDGE,"E0.0.13");
            var Q331;
            Q331=sQuery(id+"F0.wireOp",EDGE,"E0.0.25");
            var Q332;
            Q332=sQuery(id+"F0.wireOp",EDGE,"E0.0.55");
            var Q333;
            Q333=sQuery(id+"F0.wireOp",EDGE,"E0.0.124");
            var Q334;
            Q334=sQuery(id+"F0.wireOp",EDGE,"E0.0.57");
            var Q335;
            Q335=sQuery(id+"F0.wireOp",EDGE,"E0.0.73");
            var Q336;
            Q336=sQuery(id+"F0.wireOp",EDGE,"E0.0.77");
            var Q337;
            Q337=sQuery(id+"F0.wireOp",EDGE,"E0.0.86");
            var Q338;
            Q338=sQuery(id+"F0.wireOp",EDGE,"E0.0.88");
            var Q339;
            Q339=sQuery(id+"F0.wireOp",EDGE,"E0.0.89");
            var Q340;
            Q340=sQuery(id+"F0.wireOp",EDGE,"E0.0.101");
            var Q341;
            Q341=sQuery(id+"F0.wireOp",EDGE,"E0.0.103");
            var Q342;
            Q342=sQuery(id+"F0.wireOp",EDGE,"E0.0.119");
            var Q343;
            Q343=sQuery(id+"F0.wireOp",EDGE,"E0.0.121");
            var Q344;
            Q344=sQuery(id+"F0.wireOp",EDGE,"E0.0.122");
            var Q345;
            Q345=sQuery(id+"F0.wireOp",EDGE,"E0.0.58");
            var Q346;
            Q346=sQuery(id+"F0.wireOp",EDGE,"E0.0.70");
            var Q347;
            Q347=sQuery(id+"F0.wireOp",EDGE,"E0.0.123");
            var Q348;
            Q348=sQuery(id+"F0.wireOp",EDGE,"E0.0.61");
            var Q349;
            Q349=sQuery(id+"F0.wireOp",EDGE,"E0.0.120");
            var Q350;
            Q350=sQuery(id+"F0.wireOp",EDGE,"E0.0.125");
            var Q351;
            Q351=sQuery(id+"F0.wireOp",EDGE,"E0.0.9");
            var Q352;
            Q352=sQuery(id+"F0.wireOp",EDGE,"E0.0.60");
            var Q353;
            Q353=sQuery(id+"F0.wireOp",EDGE,"E0.0.59");
            var Q354;
            Q354=sQuery(id+"F0.wireOp",EDGE,"E0.0.10");
            var Q355;
            Q355=sQuery(id+"F0.wireOp",EDGE,"E0.0.14");
            var Q356;
            Q356=sQuery(id+"F0.wireOp",EDGE,"E0.0.56");
            var Q357;
            Q357=sQuery(id+"F0.wireOp",EDGE,"E0.0.62");
            var Q358;
            Q358=sQuery(id+"F0.wireOp",EDGE,"E0.0.74");
            var Q359;
            Q359=sQuery(id+"F0.wireOp",EDGE,"E0.0.16");
            var Q360;
            Q360=sQuery(id+"F0.wireOp",EDGE,"E0.0.23");
            var Q361;
            Q361=sQuery(id+"F0.wireOp",EDGE,"E0.0.15");
            var Q362;
            Q362=sQuery(id+"F0.wireOp",EDGE,"E0.0.0");
            var Q363;
            Q363=sQuery(id+"F0.wireOp",EDGE,"E0.0.8");
            var Q364;
            Q364=sQuery(id+"F0.wireOp",EDGE,"E0.0.22");
            var Q365;
            Q365=sQuery(id+"F0.wireOp",EDGE,"E0.0.87");
            var Q366;
            Q366=sQuery(id+"F0.wireOp",EDGE,"E0.0.30");
            var Q367;
            Q367=sQuery(id+"F0.wireOp",EDGE,"E0.0.63");
            var Q368;
            Q368=sQuery(id+"F0.wireOp",EDGE,"E0.0.64");
            var Q369;
            Q369=sQuery(id+"F0.wireOp",EDGE,"E0.0.66");
            var Q370;
            Q370=sQuery(id+"F0.wireOp",EDGE,"E0.0.68");
            var Q371;
            Q371=sQuery(id+"F0.wireOp",EDGE,"E0.0.69");
            var Q372;
            Q372=sQuery(id+"F0.wireOp",EDGE,"E0.0.79");
            var Q373;
            Q373=sQuery(id+"F0.wireOp",EDGE,"E0.0.80");
            var Q374;
            Q374=sQuery(id+"F0.wireOp",EDGE,"E0.0.94");
            var Q375;
            Q375=sQuery(id+"F0.wireOp",EDGE,"E0.0.11");
            var Q376;
            Q376=sQuery(id+"F0.wireOp",EDGE,"E0.0.1");
            var Q377;
            Q377=sQuery(id+"F0.wireOp",EDGE,"E0.0.126");
            var Q378;
            Q378=sQuery(id+"F0.wireOp",EDGE,"E0.0.20");
            var Q379;
            Q379=sQuery(id+"F0.wireOp",EDGE,"E0.0.2");
            var Q380;
            Q380=sQuery(id+"F0.wireOp",EDGE,"E0.0.4");
            var Q381;
            Q381=sQuery(id+"F0.wireOp",EDGE,"E0.0.6");
            var Q382;
            Q382=sQuery(id+"F0.wireOp",EDGE,"E0.0.17");
            var Q383;
            Q383=sQuery(id+"F0.wireOp",EDGE,"E0.0.18");
            var Q384;
            Q384=sQuery(id+"F0.wireOp",EDGE,"E0.0.76");
            var Q385;
            Q385=sQuery(id+"F0.wireOp",EDGE,"E0.0.67");
            var Q386;
            Q386=sQuery(id+"F0.wireOp",EDGE,"E0.0.127");
            var Q387;
            Q387=sQuery(id+"F0.wireOp",EDGE,"E0.0.81");
            var Q388;
            Q388=sQuery(id+"F0.wireOp",EDGE,"E0.0.7");
            var Q389;
            Q389=sQuery(id+"F0.wireOp",EDGE,"E0.0.85");
            var Q390;
            Q390=sQuery(id+"F0.wireOp",EDGE,"E0.0.5");
            var Q391;
            Q391=sQuery(id+"F0.wireOp",EDGE,"E0.0.19");
            var Q392;
            Q392=sQuery(id+"F0.wireOp",EDGE,"E0.0.3");
            var Q393;
            Q393=sQuery(id+"F0.wireOp",EDGE,"E0.0.12");
            var Q394;
            Q394=sQuery(id+"F0.wireOp",EDGE,"E0.0.65");
            var Q395;
            Q395=sQuery(id+"F0.wireOp",EDGE,"E0.0.72");
            var Q396;
            Q396=sQuery(id+"F0.wireOp",EDGE,"E0.0.75");
            var Q397;
            Q397=sQuery(id+"F0.wireOp",EDGE,"E0.0.83");
            var Q398;
            Q398=sQuery(id+"F0.wireOp",EDGE,"E0.0.84");
            var Q399;
            Q399=sQuery(id+"F0.wireOp",EDGE,"E0.0.82");
            var Q400;
            Q400=sQuery(id+"F0.wireOp",EDGE,"E0.0.21");
            var Q401;
            Q401=sQuery(id+"F0.wireOp",EDGE,"E0.0.71");
            extrude(context, id + "F1", {"entities" : qUnion([Q0]), "surfaceEntities" : qUnion([Q1, Q2, Q3, Q4, Q5, Q6, Q7, Q8, Q9, Q10, Q11, Q12, Q13, Q14, Q15, Q16, Q17, Q18, Q19, Q20, Q21, Q22, Q23, Q24, Q25, Q26, Q27, Q28, Q29, Q30, Q31, Q32, Q33, Q34, Q35, Q36, Q37, Q38, Q39, Q40, Q41, Q42, Q43, Q44, Q45, Q46, Q47, Q48, Q49, Q50, Q51, Q52, Q53, Q54, Q55, Q56, Q57, Q58, Q59, Q60, Q61, Q62, Q63, Q64, Q65, Q66, Q67, Q68, Q69, Q70, Q71, Q72, Q73, Q74, Q75, Q76, Q77, Q78, Q79, Q80, Q81, Q82, Q83, Q84, Q85, Q86, Q87, Q88, Q89, Q90, Q91, Q92, Q93, Q94, Q95, Q96, Q97, Q98, Q99, Q100, Q101, Q102, Q103, Q104, Q105, Q106, Q107, Q108, Q109, Q110, Q111, Q112, Q113, Q114, Q115, Q116, Q117, Q118, Q119, Q120, Q121, Q122, Q123, Q124, Q125, Q126, Q127, Q128, Q129, Q130, Q131, Q132, Q133, Q134, Q135, Q136, Q137, Q138, Q139, Q140, Q141, Q142, Q143, Q144, Q145, Q146, Q147, Q148, Q149, Q150, Q151, Q152, Q153, Q154, Q155, Q156, Q157, Q158, Q159, Q160, Q161, Q162, Q163, Q164, Q165, Q166, Q167, Q168, Q169, Q170, Q171, Q172, Q173, Q174, Q175, Q176, Q177, Q178, Q179, Q180, Q181, Q182, Q183, Q184, Q185, Q186, Q187, Q188, Q189, Q190, Q191, Q192, Q193, Q194, Q195, Q196, Q197, Q198, Q199, Q200, Q201, Q202, Q203, Q204, Q205, Q206, Q207, Q208, Q209, Q210, Q211, Q212, Q213, Q214, Q215, Q216, Q217, Q218, Q219, Q220, Q221, Q222, Q223, Q224, Q225, Q226, Q227, Q228, Q229, Q230, Q231, Q232, Q233, Q234, Q235, Q236, Q237, Q238, Q239, Q240, Q241, Q242, Q243, Q244, Q245, Q246, Q247, Q248, Q249, Q250, Q251, Q252, Q253, Q254, Q255, Q256, Q257, Q258, Q259, Q260, Q261, Q262, Q263, Q264, Q265, Q266, Q267, Q268, Q269, Q270, Q271, Q272, Q273, Q274, Q275, Q276, Q277, Q278, Q279, Q280, Q281, Q282, Q283, Q284, Q285, Q286, Q287, Q288, Q289, Q290, Q291, Q292, Q293, Q294, Q295, Q296, Q297, Q298, Q299, Q300, Q301, Q302, Q303, Q304, Q305, Q306, Q307, Q308, Q309, Q310, Q311, Q312, Q313, Q314, Q315, Q316, Q317, Q318, Q319, Q320, Q321, Q322, Q323, Q324, Q325, Q326, Q327, Q328, Q329, Q330, Q331, Q332, Q333, Q334, Q335, Q336, Q337, Q338, Q339, Q340, Q341, Q342, Q343, Q344, Q345, Q346, Q347, Q348, Q349, Q350, Q351, Q352, Q353, Q354, Q355, Q356, Q357, Q358, Q359, Q360, Q361, Q362, Q363, Q364, Q365, Q366, Q367, Q368, Q369, Q370, Q371, Q372, Q373, Q374, Q375, Q376, Q377, Q378, Q379, Q380, Q381, Q382, Q383, Q384, Q385, Q386, Q387, Q388, Q389, Q390, Q391, Q392, Q393, Q394, Q395, Q396, Q397, Q398, Q399, Q400, Q401]), "depth" : 706 * mm});
        }
    });
